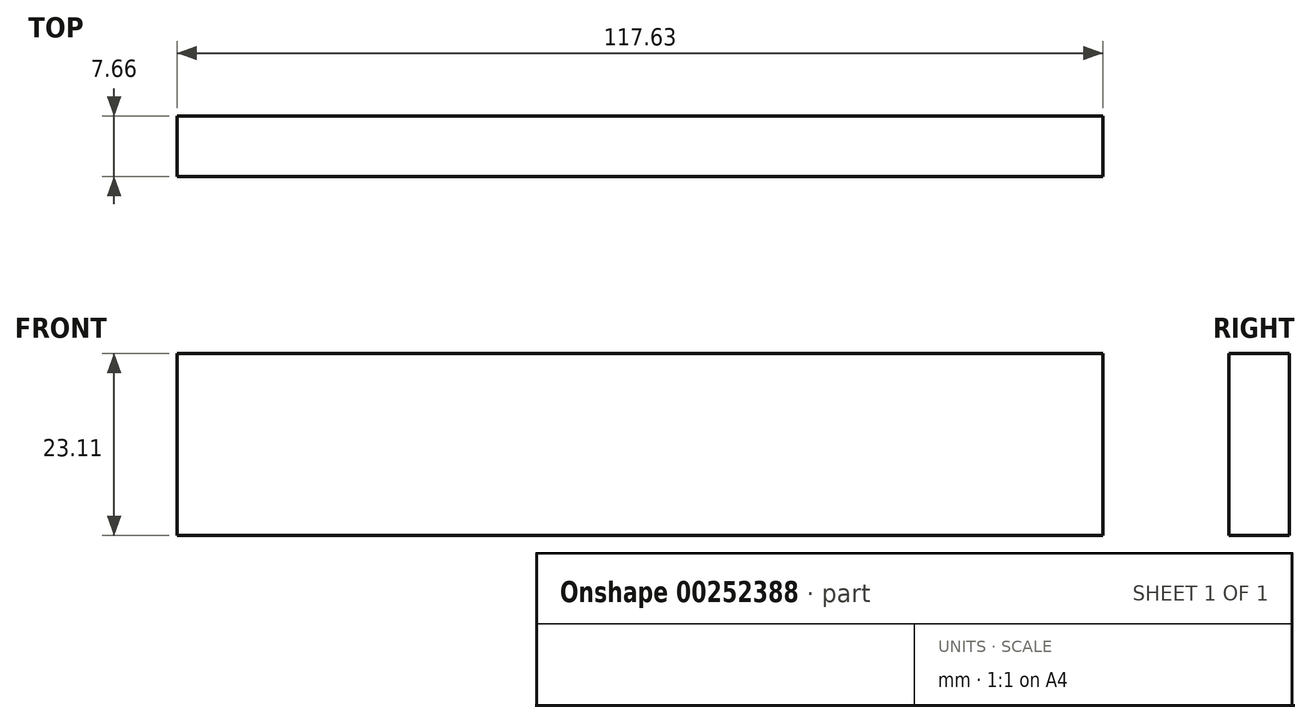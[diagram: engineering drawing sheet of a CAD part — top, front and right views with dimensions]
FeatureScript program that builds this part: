
annotation { "Feature Type Name" : "Feature", "Feature Type Description" : "" }
export const myFeature = defineFeature(function(context is Context, id is Id, definition is map)
    precondition{}
    {
        {
            var Q0;
            Q0=qCreatedBy(makeId("Front.planeOp"),FACE);
            var sketch = newSketch(context, id + "F0", { "sketchPlane" : qUnion([Q0])});
            skLineSegment(sketch, "E0.bottom", {"start": v(-59.58, 10.13) * mm, "end": v(58.05, 10.13) * mm});
            skLineSegment(sketch, "E0.top", {"start": v(-59.58, -12.98) * mm, "end": v(58.05, -12.98) * mm});
            skLineSegment(sketch, "E0.left", {"start": v(-59.58, 10.13) * mm, "end": v(-59.58, -12.98) * mm});
            skLineSegment(sketch, "E0.right", {"start": v(58.05, 10.13) * mm, "end": v(58.05, -12.98) * mm});
            skSolve(sketch);
        }
        {
            var Q0;
            Q0=makeQuery(id+"F0.imprint","IMPRINT",FACE,{"disambiguationData":[TD([[makeQuery(id+"F0.imprint","IMPRINT",EDGE,{"derivedFrom":sQuery(id+"F0.wireOp",EDGE,"E0.bottom")}),-1.0]])]});
            extrude(context, id + "F1", {"entities" : qUnion([Q0]), "endBound" : BoundingType.SYMMETRIC, "depth" : 7.65 * mm});
        }
    });
